# Revit family: spectral_stora_stora-qa-led_5200_840_mps_829e
name_source: partatom
category: Lighting Fixtures
revit_build: Autodesk Revit 2016 (Build: 20150220_1215(x64)
units: mm (PartAtom-declared; Revit-internal decimal feet)

## family parameters
Cut with Voids When Loaded = No
Host = Face
Light Source = No
Part Type = Normal
Room Calculation Point = No
Round Connector Dimension = Use Diameter
Shared = No

## types (1)
- SPECTRAL STORA (1 x )
    Apparent Load = 0 VA
    Approval mark = CE
    CIE Flux Codes = 64 90 97 96 73
    Control Gear = Electronic transformer
    Default Elevation = 1800 mm
    Description = SPC0620003
STORA surface mounted LED luminaire

Design:
Square luminaire element with microprism panel mounted in a profile frame made of power-coated aluminium. The frame is screwed to the powder-coated metal gear tray body. The underneath of the metal body accommodates the LED module formed as a square LED flat board, the top houses the electrical components The indirect lighting component is provided by recesses in the top of the metal body. Mechanical ceiling fixture to a white power-coated mounting box takes place using a connecting spring, electrical connection by means of a plug and socket system. The luminaire is configured with heatresistant wiring. Variant suitable for office workplaces with microprism panel MPS. The LED spots are visible as circles on the microprism panel. Suitable for ceiling or wall mounting. Light colours 4000 K (840) or 3000 K (830). Also in a dimmable version. Protection rating IP20, Protection class I.

Colour:
Frame – similar to RAL 9016 white silk matt
    Height = 50 mm
    Lamp = 1 x
    Lamp count = 1
    Length = 580 mm
    Luminous efficacy = 0 lm/W
    Manufacturer = Ridi
    ModVariant = No
    Model = STORA-QA-LED 5200/840 MPS
    Mounting Place = Ceiling
    Mounting Type = Surface mounted
    Number of Poles = 1
    OnlyDefault = Yes
    Power Factor = 1
    Product Name = SPECTRAL STORA
    Product group = Ceiling / wall-mounted luminaires
    ProductGroupID = 30
    Protection Class = Protection class
    Protection Degree = IP 20
    RlxData = <blob elided: 13077 chars, md5=111b0d48>
    Socket = socket
    Standby Power = 0 W
    System Light Flux = 0 lm
    System Power = 0 W
    Type Image = stora-qa_512.jpg
    URL = http://reluxnet.relux.com
    VarID = 1
    Voltage = 0 V
    Weight = 0.00 kg
    Width = 580 mm

## geometry (parser evidence)
native form markers: Sweep x7
no freeform markers — native parametric forms only
